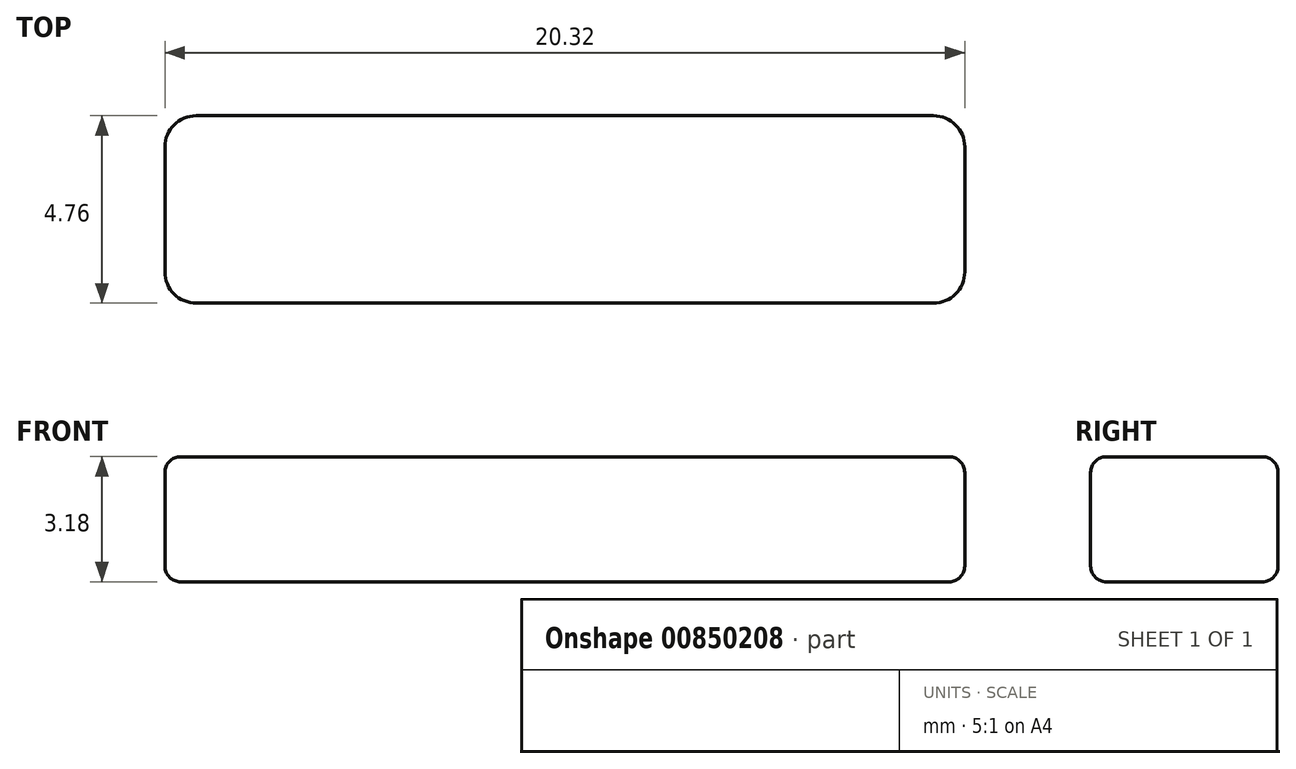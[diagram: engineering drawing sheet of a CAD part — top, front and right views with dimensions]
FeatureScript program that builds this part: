
annotation { "Feature Type Name" : "Feature", "Feature Type Description" : "" }
export const myFeature = defineFeature(function(context is Context, id is Id, definition is map)
    precondition{}
    {
        {
            var Q0;
            Q0=qCreatedBy(makeId("Top.planeOp"),FACE);
            var sketch = newSketch(context, id + "F0", { "sketchPlane" : qUnion([Q0])});
            skLineSegment(sketch, "E0.left", {"start": v(2.38, 2.38) * mm, "end": v(2.38, -2.38) * mm});
            skLineSegment(sketch, "E0.right", {"start": v(-2.38, 2.38) * mm, "end": v(-2.38, -2.38) * mm});
            skPoint(sketch, "E0.middle", {"position": v(0, 0) * mm});
            skLineSegment(sketch, "E1.bottom", {"start": v(9.37, 2.38) * mm, "end": v(-9.37, 2.38) * mm});
            skLineSegment(sketch, "E1.top", {"start": v(9.37, -2.38) * mm, "end": v(-9.37, -2.38) * mm});
            skLineSegment(sketch, "E1.left", {"start": v(10.16, 1.59) * mm, "end": v(10.16, -1.59) * mm});
            skLineSegment(sketch, "E1.right", {"start": v(-10.16, 1.59) * mm, "end": v(-10.16, -1.59) * mm});
            skPoint(sketch, "E2.visualSharp", {"position": v(10.16, 2.38) * mm});
            skArc(sketch, "E2.filletArc", {"start": v(10.16, 1.59) * mm, "mid": v(9.93, 2.15) * mm, "end": v(9.37, 2.38) * mm});
            skPoint(sketch, "E3.visualSharp", {"position": v(10.16, -2.38) * mm});
            skArc(sketch, "E3.filletArc", {"start": v(9.37, -2.38) * mm, "mid": v(9.93, -2.15) * mm, "end": v(10.16, -1.59) * mm});
            skPoint(sketch, "E4.visualSharp", {"position": v(-10.16, -2.38) * mm});
            skArc(sketch, "E4.filletArc", {"start": v(-10.16, -1.59) * mm, "mid": v(-9.93, -2.15) * mm, "end": v(-9.37, -2.38) * mm});
            skPoint(sketch, "E5.visualSharp", {"position": v(-10.16, 2.38) * mm});
            skArc(sketch, "E5.filletArc", {"start": v(-9.37, 2.38) * mm, "mid": v(-9.93, 2.15) * mm, "end": v(-10.16, 1.59) * mm});
            skSolve(sketch);
        }
        {
            var Q0;
            Q0 = qSketchRegion(id + "F0", true);
            extrude(context, id + "F1", {"entities" : qUnion([Q0]), "depth" : 3.17 * mm, "offsetDistance" : 25.4 * mm});
        }
        {
            var Q0;
            Q0=makeQuery(id+"F1.opExtrude","CAP_FACE",FACE,{"disambiguationData":[OSD([sQuery(id+"F0.wireOp",EDGE,"E0.bottom"),sQuery(id+"F0.wireOp",EDGE,"E0.top"),sQuery(id+"F0.wireOp",EDGE,"E0.left"),sQuery(id+"F0.wireOp",EDGE,"E0.right"),sQuery(id+"F0.wireOp",EDGE,"E1.bottom"),sQuery(id+"F0.wireOp",EDGE,"E1.top"),sQuery(id+"F0.wireOp",EDGE,"E1.left"),sQuery(id+"F0.wireOp",EDGE,"E1.right"),sQuery(id+"F0.wireOp",EDGE,"e48c8cea-de37-4d7b-bebe-fad5d6120350.filletArc"),sQuery(id+"F0.wireOp",EDGE,"ac0e0184-b8f9-40ee-be1f-0dbaa781b01f.filletArc"),sQuery(id+"F0.wireOp",EDGE,"E2.filletArc"),sQuery(id+"F0.wireOp",EDGE,"E3.filletArc"),sQuery(id+"F0.wireOp",EDGE,"b21ffb10-67be-451b-972d-374475a50460.filletArc"),sQuery(id+"F0.wireOp",EDGE,"21edf1ef-150f-4090-9226-d487b1d7afae.filletArc"),sQuery(id+"F0.wireOp",EDGE,"E4.filletArc"),sQuery(id+"F0.wireOp",EDGE,"E5.filletArc")])],"isStart":false});
            var Q1;
            Q1=makeQuery(id+"F1.opExtrude","CAP_FACE",FACE,{"disambiguationData":[OSD([sQuery(id+"F0.wireOp",EDGE,"E0.bottom"),sQuery(id+"F0.wireOp",EDGE,"E0.top"),sQuery(id+"F0.wireOp",EDGE,"E0.left"),sQuery(id+"F0.wireOp",EDGE,"E0.right"),sQuery(id+"F0.wireOp",EDGE,"E1.bottom"),sQuery(id+"F0.wireOp",EDGE,"E1.top"),sQuery(id+"F0.wireOp",EDGE,"E1.left"),sQuery(id+"F0.wireOp",EDGE,"E1.right"),sQuery(id+"F0.wireOp",EDGE,"e48c8cea-de37-4d7b-bebe-fad5d6120350.filletArc"),sQuery(id+"F0.wireOp",EDGE,"ac0e0184-b8f9-40ee-be1f-0dbaa781b01f.filletArc"),sQuery(id+"F0.wireOp",EDGE,"E2.filletArc"),sQuery(id+"F0.wireOp",EDGE,"E3.filletArc"),sQuery(id+"F0.wireOp",EDGE,"b21ffb10-67be-451b-972d-374475a50460.filletArc"),sQuery(id+"F0.wireOp",EDGE,"21edf1ef-150f-4090-9226-d487b1d7afae.filletArc"),sQuery(id+"F0.wireOp",EDGE,"E4.filletArc"),sQuery(id+"F0.wireOp",EDGE,"E5.filletArc")])],"isStart":true});
            fillet(context, id + "F2", {"entities" : qUnion([Q0, Q1]), "tangentPropagation" : true, "radius" : 0.4 * mm, "defaultsChanged" : false, "vertexSettings" : [], "allowEdgeOverflow" : false});
        }
    });
